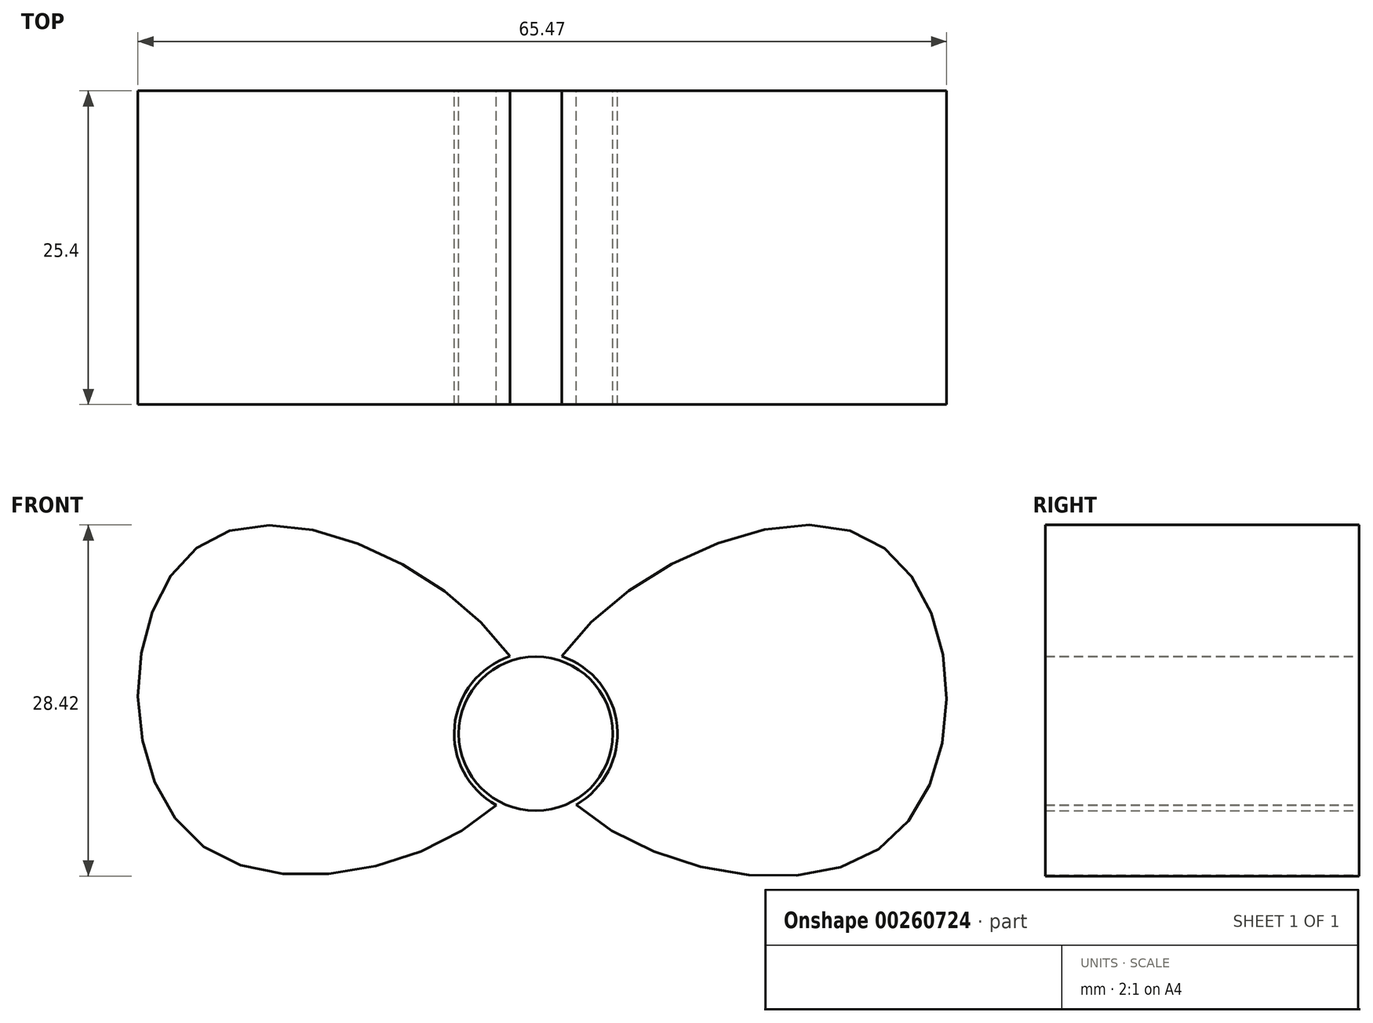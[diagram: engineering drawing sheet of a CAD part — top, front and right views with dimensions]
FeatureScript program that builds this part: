
annotation { "Feature Type Name" : "Feature", "Feature Type Description" : "" }
export const myFeature = defineFeature(function(context is Context, id is Id, definition is map)
    precondition{}
    {
        {
            var Q0;
            Q0=qCreatedBy(makeId("Front.planeOp"),FACE);
            var sketch = newSketch(context, id + "F0", { "sketchPlane" : qUnion([Q0])});
            skCircle(sketch, "E0", {"center": v(0, 0) * mm, "radius": 6.6 * mm});
            skFitSpline(sketch, "E1", {"points": [v(0, 0) * mm, v(-25.77, 16.05) * mm, v(-26.7, -9.25) * mm, v(0, 0) * mm]});
            skFitSpline(sketch, "E2", {"points": [v(0, 0) * mm, v(26.47, 16.05) * mm, v(27.88, -9.25) * mm, v(0, 0) * mm]});
            skSolve(sketch);
        }
        {
            var Q0;
            {var subQ0=sQuery(id+"F0.wireOp",EDGE,"E1");var subQ1=sQuery(id+"F0.wireOp",EDGE,"E0");var subQ2=makeQuery(id+"F0.imprint","INTERSECT",VERTEX,{"disambiguationData":[OD(0.0)],"derivedFrom":[subQ1,subQ0]});Q0=makeQuery(id+"F0.imprint","IMPRINT",FACE,{"disambiguationData":[TD([[makeQuery(id+"F0.imprint","IMPRINT",EDGE,{"disambiguationData":[TD([[subQ2,-1.0]])],"derivedFrom":subQ1}),-1.0]])]});}
            var Q1;
            {var subQ0=sQuery(id+"F0.wireOp",EDGE,"E2");var subQ1=sQuery(id+"F0.wireOp",EDGE,"E0");var subQ2=makeQuery(id+"F0.imprint","INTERSECT",VERTEX,{"disambiguationData":[OD(0.0)],"derivedFrom":[subQ1,subQ0]});Q1=makeQuery(id+"F0.imprint","IMPRINT",FACE,{"disambiguationData":[TD([[makeQuery(id+"F0.imprint","IMPRINT",EDGE,{"disambiguationData":[TD([[subQ2,1.0]])],"derivedFrom":subQ1}),-1.0]])]});}
            extrude(context, id + "F1", {"entities" : qUnion([Q0, Q1]), "depth" : 25.4 * mm});
        }
        {
            var Q0;
            Q0=qCreatedBy(makeId("Front.planeOp"),FACE);
            var sketch = newSketch(context, id + "F2", { "sketchPlane" : qUnion([Q0])});
            skCircle(sketch, "E3", {"center": v(0, 0) * mm, "radius": 6.23 * mm});
            skSolve(sketch);
        }
        {
            var Q0;
            Q0=makeQuery(id+"F2.imprint","IMPRINT",FACE,{"disambiguationData":[TD([[makeQuery(id+"F2.imprint","IMPRINT",EDGE,{"derivedFrom":sQuery(id+"F2.wireOp",EDGE,"E3")}),1.0]])]});
            extrude(context, id + "F3", {"entities" : qUnion([Q0]), "depth" : 25.4 * mm});
        }
    });
